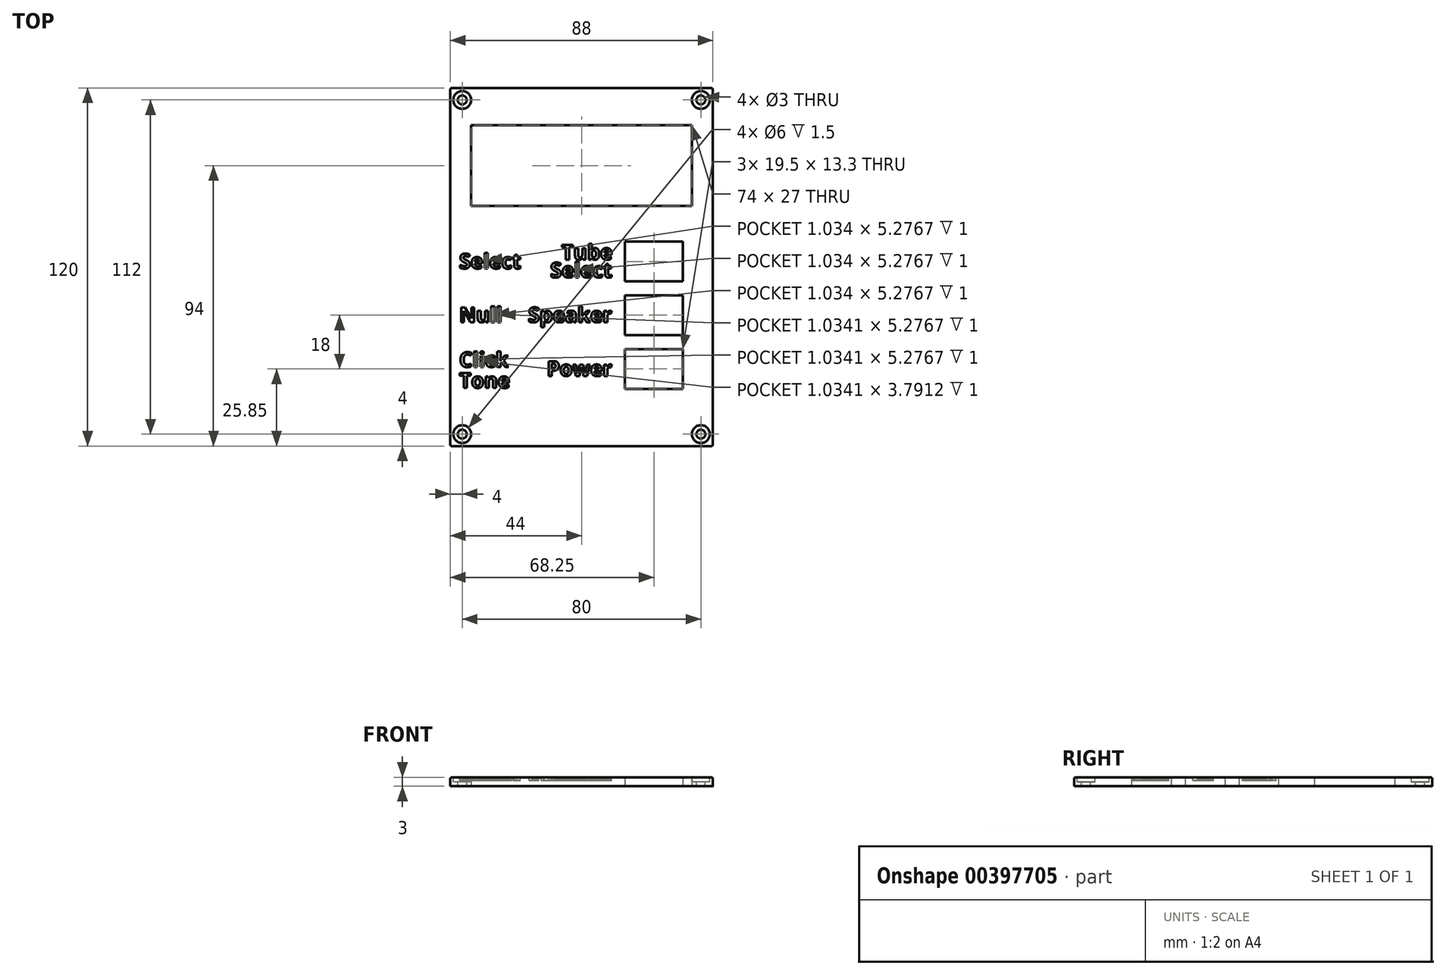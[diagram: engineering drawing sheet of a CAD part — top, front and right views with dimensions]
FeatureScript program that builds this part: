
annotation { "Feature Type Name" : "Feature", "Feature Type Description" : "" }
export const myFeature = defineFeature(function(context is Context, id is Id, definition is map)
    precondition{}
    {
        {
            var Q0;
            Q0=qCreatedBy(makeId("Top.planeOp"),FACE);
            var sketch = newSketch(context, id + "F0", { "sketchPlane" : qUnion([Q0])});
            skLineSegment(sketch, "E0.bottom", {"start": v(0, 0) * mm, "end": v(88, 0) * mm});
            skLineSegment(sketch, "E0.top", {"start": v(0, 120) * mm, "end": v(88, 120) * mm});
            skLineSegment(sketch, "E0.left", {"start": v(0, 0) * mm, "end": v(0, 120) * mm});
            skLineSegment(sketch, "E0.right", {"start": v(88, 0) * mm, "end": v(88, 120) * mm});
            skLineSegment(sketch, "E1.bottom", {"start": v(7, 107.5) * mm, "end": v(81, 107.5) * mm});
            skLineSegment(sketch, "E1.top", {"start": v(7, 80.5) * mm, "end": v(81, 80.5) * mm});
            skLineSegment(sketch, "E1.left", {"start": v(7, 107.5) * mm, "end": v(7, 80.5) * mm});
            skLineSegment(sketch, "E1.right", {"start": v(81, 107.5) * mm, "end": v(81, 80.5) * mm});
            skPoint(sketch, "E2", {"position": v(44, 120) * mm});
            skPoint(sketch, "E3", {"position": v(44, 107.5) * mm});
            skLineSegment(sketch, "E4", {"start": v(44, 120) * mm, "end": v(44, 107.5) * mm, "construction": true});
            skLineSegment(sketch, "E5.bottom", {"start": v(58.5, 68.5) * mm, "end": v(78, 68.5) * mm});
            skLineSegment(sketch, "E5.top", {"start": v(58.5, 55.2) * mm, "end": v(78, 55.2) * mm});
            skLineSegment(sketch, "E5.left", {"start": v(58.5, 68.5) * mm, "end": v(58.5, 55.2) * mm});
            skLineSegment(sketch, "E5.right", {"start": v(78, 68.5) * mm, "end": v(78, 55.2) * mm});
            skLineSegment(sketch, "E6.0.1.0", {"start": v(78, 50.5) * mm, "end": v(78, 37.2) * mm});
            skLineSegment(sketch, "E6.0.1.1", {"start": v(58.5, 50.5) * mm, "end": v(58.5, 37.2) * mm});
            skLineSegment(sketch, "E6.0.1.2", {"start": v(58.5, 37.2) * mm, "end": v(78, 37.2) * mm});
            skLineSegment(sketch, "E6.0.1.3", {"start": v(58.5, 50.5) * mm, "end": v(78, 50.5) * mm});
            skLineSegment(sketch, "E6.0.2.0", {"start": v(78, 32.5) * mm, "end": v(78, 19.2) * mm});
            skLineSegment(sketch, "E6.0.2.1", {"start": v(58.5, 32.5) * mm, "end": v(58.5, 19.2) * mm});
            skLineSegment(sketch, "E6.0.2.2", {"start": v(58.5, 19.2) * mm, "end": v(78, 19.2) * mm});
            skLineSegment(sketch, "E6.0.2.3", {"start": v(58.5, 32.5) * mm, "end": v(78, 32.5) * mm});
            skLineSegment(sketch, "E6.direction1", {"start": v(58.5, 55.2) * mm, "end": v(81.29, 55.2) * mm, "construction": true});
            skLineSegment(sketch, "E6.direction2", {"start": v(58.5, 55.2) * mm, "end": v(58.5, 37.2) * mm, "construction": true});
            skSolve(sketch);
        }
        {
            var Q0;
            Q0=makeQuery(id+"F0.imprint","IMPRINT",FACE,{"disambiguationData":[TD([[makeQuery(id+"F0.imprint","IMPRINT",EDGE,{"derivedFrom":sQuery(id+"F0.wireOp",EDGE,"E0.bottom")}),1.0]])]});
            extrude(context, id + "F1", {"entities" : qUnion([Q0]), "depth" : 3 * mm});
        }
        {
            var Q0;
            Q0=makeQuery(id+"F1.opExtrude","CAP_FACE",FACE,{"disambiguationData":[OSD([sQuery(id+"F0.wireOp",EDGE,"E0.bottom"),sQuery(id+"F0.wireOp",EDGE,"E0.top"),sQuery(id+"F0.wireOp",EDGE,"E0.left"),sQuery(id+"F0.wireOp",EDGE,"E0.right"),sQuery(id+"F0.wireOp",EDGE,"E1.bottom"),sQuery(id+"F0.wireOp",EDGE,"E1.top"),sQuery(id+"F0.wireOp",EDGE,"E1.left"),sQuery(id+"F0.wireOp",EDGE,"E1.right"),sQuery(id+"F0.wireOp",EDGE,"E5.bottom"),sQuery(id+"F0.wireOp",EDGE,"E5.top"),sQuery(id+"F0.wireOp",EDGE,"E5.left"),sQuery(id+"F0.wireOp",EDGE,"E5.right"),sQuery(id+"F0.wireOp",EDGE,"E6.0.1.0"),sQuery(id+"F0.wireOp",EDGE,"E6.0.1.1"),sQuery(id+"F0.wireOp",EDGE,"E6.0.1.2"),sQuery(id+"F0.wireOp",EDGE,"E6.0.1.3"),sQuery(id+"F0.wireOp",EDGE,"E6.0.2.0"),sQuery(id+"F0.wireOp",EDGE,"E6.0.2.1"),sQuery(id+"F0.wireOp",EDGE,"E6.0.2.2"),sQuery(id+"F0.wireOp",EDGE,"E6.0.2.3")])],"isStart":false});
            var sketch = newSketch(context, id + "F2", { "sketchPlane" : qUnion([Q0])});
            skPoint(sketch, "E7", {"position": v(4, 116) * mm});
            skPoint(sketch, "E8", {"position": v(4, 4) * mm});
            skPoint(sketch, "E9", {"position": v(84, 4) * mm});
            skPoint(sketch, "E10", {"position": v(84, 116) * mm});
            skLineSegment(sketch, "E11", {"start": v(4, 116) * mm, "end": v(84, 116) * mm, "construction": true});
            skLineSegment(sketch, "E12", {"start": v(84, 116) * mm, "end": v(84, 4) * mm, "construction": true});
            skLineSegment(sketch, "E13", {"start": v(84, 4) * mm, "end": v(4, 4) * mm, "construction": true});
            skLineSegment(sketch, "E14", {"start": v(4, 4) * mm, "end": v(4, 116) * mm, "construction": true});
            skSolve(sketch);
        }
        {
            var Q0;
            Q0=sQuery(id+"F2.wireOp",VERTEX,"E7");
            var Q1;
            Q1=sQuery(id+"F2.wireOp",VERTEX,"E10");
            var Q2;
            Q2=sQuery(id+"F2.wireOp",VERTEX,"E9");
            var Q3;
            Q3=sQuery(id+"F2.wireOp",VERTEX,"E8");
            var Q4;
            Q4=makeQuery(id+"F1.opExtrude","SWEPT_BODY",BODY,{"disambiguationData":[OSD([sQuery(id+"F0.wireOp",EDGE,"E0.bottom"),sQuery(id+"F0.wireOp",EDGE,"E0.top"),sQuery(id+"F0.wireOp",EDGE,"E0.left"),sQuery(id+"F0.wireOp",EDGE,"E0.right"),sQuery(id+"F0.wireOp",EDGE,"E1.bottom"),sQuery(id+"F0.wireOp",EDGE,"E1.top"),sQuery(id+"F0.wireOp",EDGE,"E1.left"),sQuery(id+"F0.wireOp",EDGE,"E1.right"),sQuery(id+"F0.wireOp",EDGE,"E5.bottom"),sQuery(id+"F0.wireOp",EDGE,"E5.top"),sQuery(id+"F0.wireOp",EDGE,"E5.left"),sQuery(id+"F0.wireOp",EDGE,"E5.right"),sQuery(id+"F0.wireOp",EDGE,"E6.0.1.0"),sQuery(id+"F0.wireOp",EDGE,"E6.0.1.1"),sQuery(id+"F0.wireOp",EDGE,"E6.0.1.2"),sQuery(id+"F0.wireOp",EDGE,"E6.0.1.3"),sQuery(id+"F0.wireOp",EDGE,"E6.0.2.0"),sQuery(id+"F0.wireOp",EDGE,"E6.0.2.1"),sQuery(id+"F0.wireOp",EDGE,"E6.0.2.2"),sQuery(id+"F0.wireOp",EDGE,"E6.0.2.3")])]});
            hole(context, id + "F3", {"style" : HoleStyle.C_BORE, "endStyle" : HoleEndStyle.THROUGH, "holeDiameter" : 3 * mm, "cBoreDiameter" : 6 * mm, "cBoreDepth" : 1.5 * mm, "isTappedThrough" : true, "tappedDepth" : 12 * mm, "tapClearance" : 3, "locations" : qUnion([Q0, Q1, Q2, Q3]), "scope" : qUnion([Q4])});
        }
        {
            var Q0;
            Q0=makeQuery(id+"F1.opExtrude","CAP_FACE",FACE,{"disambiguationData":[OSD([sQuery(id+"F0.wireOp",EDGE,"E0.bottom"),sQuery(id+"F0.wireOp",EDGE,"E0.top"),sQuery(id+"F0.wireOp",EDGE,"E0.left"),sQuery(id+"F0.wireOp",EDGE,"E0.right"),sQuery(id+"F0.wireOp",EDGE,"E1.bottom"),sQuery(id+"F0.wireOp",EDGE,"E1.top"),sQuery(id+"F0.wireOp",EDGE,"E1.left"),sQuery(id+"F0.wireOp",EDGE,"E1.right"),sQuery(id+"F0.wireOp",EDGE,"E5.bottom"),sQuery(id+"F0.wireOp",EDGE,"E5.top"),sQuery(id+"F0.wireOp",EDGE,"E5.left"),sQuery(id+"F0.wireOp",EDGE,"E5.right"),sQuery(id+"F0.wireOp",EDGE,"E6.0.1.0"),sQuery(id+"F0.wireOp",EDGE,"E6.0.1.1"),sQuery(id+"F0.wireOp",EDGE,"E6.0.1.2"),sQuery(id+"F0.wireOp",EDGE,"E6.0.1.3"),sQuery(id+"F0.wireOp",EDGE,"E6.0.2.0"),sQuery(id+"F0.wireOp",EDGE,"E6.0.2.1"),sQuery(id+"F0.wireOp",EDGE,"E6.0.2.2"),sQuery(id+"F0.wireOp",EDGE,"E6.0.2.3")])],"isStart":false});
            var sketch = newSketch(context, id + "F4", { "sketchPlane" : qUnion([Q0])});
            skText(sketch, "E15", { "text": "Tube", "fontName": "OpenSans-Bold.ttf"});
            skText(sketch, "E16", { "text": "Select", "fontName": "OpenSans-Bold.ttf"});
            skText(sketch, "E17", { "text": "Power", "fontName": "OpenSans-Bold.ttf"});
            skText(sketch, "E18", { "text": "Speaker", "fontName": "OpenSans-Bold.ttf"});
            skText(sketch, "E19", { "text": "Select", "fontName": "OpenSans-Bold.ttf"});
            skText(sketch, "E20", { "text": "Null", "fontName": "OpenSans-Bold.ttf"});
            skText(sketch, "E21", { "text": "Click", "fontName": "OpenSans-Bold.ttf"});
            skText(sketch, "E22", { "text": "Tone", "fontName": "OpenSans-Bold.ttf"});
            const initialGuessF4  = {"E15": [0.03727, 0.0625, 1, 0, 0.005], "E16": [0.03354, 0.0565, 1, 0, 0.005], "E17": [0.03233, 0.0235, 1, 0, 0.005], "E18": [0.02612, 0.0415, 1, 0, 0.005], "E19": [0.003, 0.0595, 1, 0, 0.005], "E20": [0.003, 0.0415, 1, 0, 0.005], "E21": [0.003, 0.0265, 1, 0, 0.005], "E22": [0.003, 0.0195, 1, 0, 0.005]};
            skSetInitialGuess(sketch, initialGuessF4);
            skSolve(sketch);
        }
        {
            var Q0;
            Q0 = qSketchRegion(id + "F4", true);
            extrude(context, id + "F5", {"entities" : qUnion([Q0]), "operationType" : NewBodyOperationType.REMOVE, "oppositeDirection" : true, "depth" : 1 * mm});
        }
        {
            var Q0;
            Q0=makeQuery(id+"F1.opExtrude","CAP_EDGE",EDGE,{"disambiguationData":[OSD([sQuery(id+"F0.wireOp",EDGE,"E0.left")])],"isStart":false});
            var Q1;
            Q1=makeQuery(id+"F1.opExtrude","CAP_EDGE",EDGE,{"disambiguationData":[OSD([sQuery(id+"F0.wireOp",EDGE,"E0.top")])],"isStart":false});
            var Q2;
            Q2=makeQuery(id+"F1.opExtrude","CAP_EDGE",EDGE,{"disambiguationData":[OSD([sQuery(id+"F0.wireOp",EDGE,"E0.right")])],"isStart":false});
            var Q3;
            Q3=makeQuery(id+"F1.opExtrude","CAP_EDGE",EDGE,{"disambiguationData":[OSD([sQuery(id+"F0.wireOp",EDGE,"E0.bottom")])],"isStart":false});
            var Q4;
            Q4=makeQuery(id+"F1.opExtrude","SWEPT_EDGE",EDGE,{"disambiguationData":[OSD([sQuery(id+"F0.wireOp",EDGE,"E0.bottom"),sQuery(id+"F0.wireOp",EDGE,"E0.left")])]});
            var Q5;
            Q5=makeQuery(id+"F1.opExtrude","SWEPT_EDGE",EDGE,{"disambiguationData":[OSD([sQuery(id+"F0.wireOp",EDGE,"E0.bottom"),sQuery(id+"F0.wireOp",EDGE,"E0.right")])]});
            var Q6;
            Q6=makeQuery(id+"F1.opExtrude","SWEPT_EDGE",EDGE,{"disambiguationData":[OSD([sQuery(id+"F0.wireOp",EDGE,"E0.top"),sQuery(id+"F0.wireOp",EDGE,"E0.left")])]});
            var Q7;
            Q7=makeQuery(id+"F1.opExtrude","SWEPT_EDGE",EDGE,{"disambiguationData":[OSD([sQuery(id+"F0.wireOp",EDGE,"E0.top"),sQuery(id+"F0.wireOp",EDGE,"E0.right")])]});
            fillet(context, id + "F6", {"entities" : qUnion([Q0, Q1, Q2, Q3, Q4, Q5, Q6, Q7]), "radius" : 0.5 * mm, "tangentPropagation" : true, "allowEdgeOverflow" : false});
        }
    });
